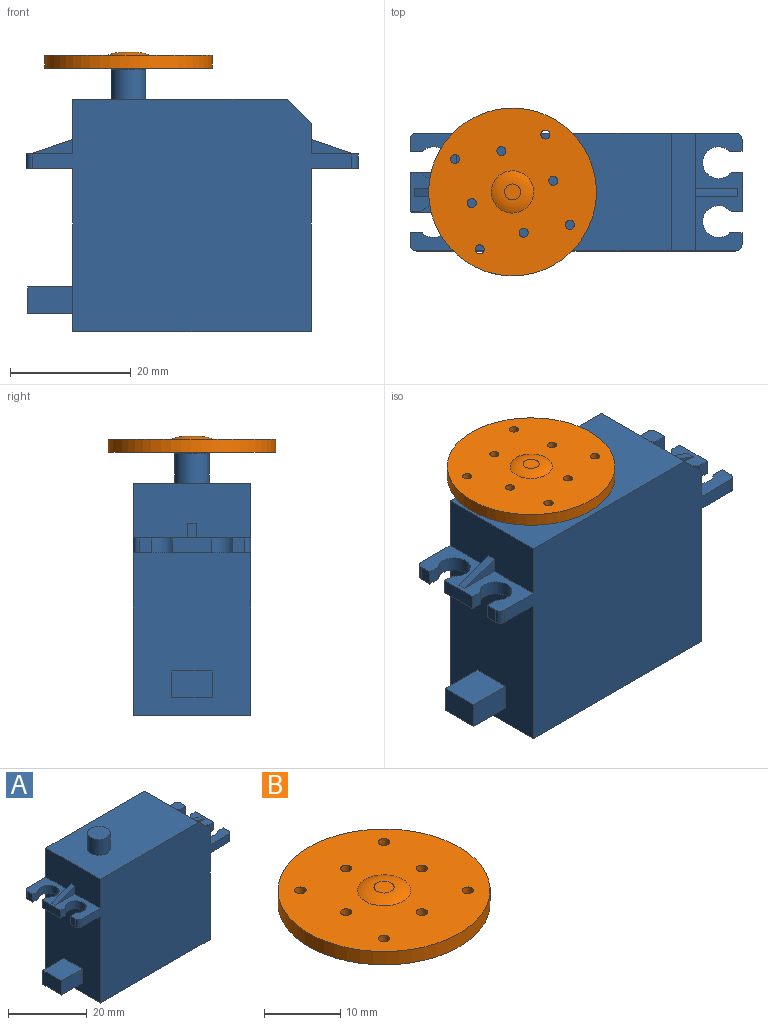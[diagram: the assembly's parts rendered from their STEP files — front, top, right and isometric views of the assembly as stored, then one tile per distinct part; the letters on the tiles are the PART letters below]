
ASSEMBLY  parts=2 mates=1
PART A: 48 faces, bbox 55x19.5x43.4 mm
  f0: plane 19.5x7.75mm, normal (0,0,1), area 87.7mm2, adj f1,f6,f7,f23,f24,f25,f26,f27
  f1: plane 19.5x9.06mm, normal (-1,0,0), area 173.4mm2, adj f0,f6,f7,f8,f45,f46,f47
  f2: plane 19.5x7.75mm, normal (0,0,1), area 87.7mm2, adj f5,f6,f7,f11,f12,f13,f14,f15
  f3: plane 27x19.5mm, normal (-1,0,0), area 497mm2, adj f6,f7,f9,f32,f35,f36,f37,f38
  f4: plane 27x19.5mm, normal (1,0,0), area 526.5mm2, adj f6,f7,f9,f20
  f5: plane 19.5x5.06mm, normal (1,0,0), area 95.4mm2, adj f2,f6,f7,f10,f42,f43,f44
  f6: plane 53x38.5mm, normal (0,1,0), area 1545.7mm2, adj f0,f1,f2,f3,f4,f5,f8,f9
  f7: plane 53x38.5mm, normal (0,-1,0), area 1545.7mm2, adj f0,f1,f2,f3,f4,f5,f8,f9
  f8: plane 35.5x19.5mm, normal (0,0,1), area 666.1mm2, adj f1,f6,f7,f10,f40
  f9: plane 39.5x19.5mm, normal (0,0,-1), area 770.2mm2, adj f3,f4,f6,f7
  f10: plane 19.5x4mm, normal (0.71,0,0.71), area 110.3mm2, adj f5,f6,f7,f8
  f11: plane 2.44x1.79mm, normal (0,1,0), area 4.4mm2, adj f2,f12,f19,f20
  f12: cylinder r=2.62mm len=5.25mm, axis (0,0,-1), area 31mm2, adj f2,f11,f13,f20
  f13: plane 2.44x2.04mm, normal (0,-1,0), area 5mm2, adj f2,f12,f14,f20
  f14: plane 2.44x2mm, normal (1,0,0), area 4.9mm2, adj f2,f13,f20,f21
  f15: plane 2.44x2mm, normal (1,0,0), area 4.9mm2, adj f2,f16,f20,f22
  f16: plane 2.44x2.04mm, normal (0,1,0), area 5mm2, adj f2,f15,f17,f20
  f17: cylinder r=2.62mm len=5.25mm, axis (0,0,-1), area 31mm2, adj f2,f16,f18,f20
  f18: plane 2.44x1.79mm, normal (0,-1,0), area 4.4mm2, adj f2,f17,f19,f20
  f19: plane 6.55x2.44mm, normal (1,0,0), area 16mm2, adj f2,f11,f18,f20
  f20: plane 19.5x7.75mm, normal (0,0,-1), area 97.2mm2, adj f4,f6,f7,f11,f12,f13,f14,f15
  f21: cylinder r=1mm len=2.44mm, axis (0,0,-1), area 3.8mm2, adj f2,f6,f14,f20
  f22: cylinder r=1mm len=2.44mm, axis (0,0,1), area 3.8mm2, adj f2,f7,f15,f20
  f23: plane 2.44x1.79mm, normal (0,1,0), area 4.4mm2, adj f0,f24,f31,f32
  f24: plane 6.55x2.44mm, normal (-1,0,0), area 16mm2, adj f0,f23,f25,f32
  f25: plane 2.44x1.79mm, normal (0,-1,0), area 4.4mm2, adj f0,f24,f26,f32
  f26: cylinder r=2.62mm len=5.25mm, axis (0,0,-1), area 31mm2, adj f0,f25,f27,f32
  f27: plane 2.44x2.04mm, normal (0,1,0), area 5mm2, adj f0,f26,f28,f32
  f28: plane 2.44x2mm, normal (-1,0,0), area 4.9mm2, adj f0,f27,f32,f34
  f29: plane 2.44x2mm, normal (-1,0,0), area 4.9mm2, adj f0,f30,f32,f33
  f30: plane 2.44x2.04mm, normal (0,-1,0), area 5mm2, adj f0,f29,f31,f32
  f31: cylinder r=2.62mm len=5.25mm, axis (0,0,-1), area 31mm2, adj f0,f23,f30,f32
  f32: plane 19.5x7.75mm, normal (0,0,-1), area 97.2mm2, adj f3,f6,f7,f23,f24,f25,f26,f27
  f33: cylinder r=1mm len=2.44mm, axis (0,0,1), area 3.8mm2, adj f0,f6,f29,f32
  f34: cylinder r=1mm len=2.44mm, axis (0,0,-1), area 3.8mm2, adj f0,f7,f28,f32
  f35: plane 7.5x6.7mm, normal (0,0,-1), area 50.2mm2, adj f3,f36,f38,f39
  f36: plane 7.5x4.4mm, normal (0,-1,0), area 33mm2, adj f3,f35,f37,f39
  f37: plane 7.5x6.7mm, normal (0,0,1), area 50.2mm2, adj f3,f36,f38,f39
  f38: plane 7.5x4.4mm, normal (0,1,0), area 33mm2, adj f3,f35,f37,f39
  f39: plane 6.7x4.4mm, normal (-1,0,0), area 29.5mm2, adj f35,f36,f37,f38
  f40: cylinder r=2.88mm len=5.77mm, axis (0,0,-1), area 89.5mm2, adj f8,f41
  f41: plane 5.77x5.77mm, normal (0,0,1), area 26.1mm2, adj f40
  f42: plane 7.05x2.41mm, normal (0,-1,0), area 8.5mm2, adj f2,f5,f44
  f43: plane 7.05x2.41mm, normal (0,1,0), area 8.5mm2, adj f2,f5,f44
  f44: plane 7.05x2.41mm, normal (0.32,0,0.95), area 10.1mm2, adj f2,f5,f42,f43
  f45: plane 7.05x2.41mm, normal (0,1,0), area 8.5mm2, adj f0,f1,f47
  f46: plane 7.05x2.41mm, normal (0,-1,0), area 8.5mm2, adj f0,f1,f47
  f47: plane 7.05x2.41mm, normal (-0.32,0,0.95), area 10.1mm2, adj f0,f1,f45,f46
PART B: 13 faces, bbox 27.8x27.8x2.6 mm
  f0: cylinder r=0.75mm len=2.14mm, axis (0,0,1), area 10.1mm2, adj f9,f10
  f1: cylinder r=0.75mm len=2.14mm, axis (0,0,1), area 10.1mm2, adj f9,f10
  f2: cylinder r=0.75mm len=2.14mm, axis (0,0,1), area 10.1mm2, adj f9,f10
  f3: cylinder r=0.75mm len=2.14mm, axis (0,0,1), area 10.1mm2, adj f9,f10
  f4: cylinder r=0.75mm len=2.14mm, axis (0,0,1), area 10.1mm2, adj f9,f10
  f5: cylinder r=0.75mm len=2.14mm, axis (0,0,1), area 10.1mm2, adj f9,f10
  f6: cylinder r=0.75mm len=2.14mm, axis (0,0,1), area 10.1mm2, adj f9,f10
  f7: cylinder r=0.75mm len=2.14mm, axis (0,0,1), area 10.1mm2, adj f9,f10
  f8: cylinder r=13.89mm len=27.78mm, axis (0,0,1), area 186.8mm2, adj f9,f10
  f9: plane 27.78x27.78mm, normal (0,0,-1), area 592mm2, adj f0,f1,f2,f3,f4,f5,f6,f7
  f10: plane 27.78x27.78mm, normal (0,0,1), area 553.5mm2, adj f0,f1,f2,f3,f4,f5,f6,f7
  f11: plane 2.64x2.64mm, normal (0,0,1), area 5.5mm2, adj f12
  f12: torus R=1.32mm, axis (0,0,-1), area 34.4mm2, adj f10,f11
PLACE A at identity fixed
PLACE B rot(axis=(0,0,-1),74.8deg) t=(-7.75,-10.15,0)mm
MATE revolute B.f8 <-> A.f40  axis (0,0,-1) through (-10.51,0,43.63)mm
